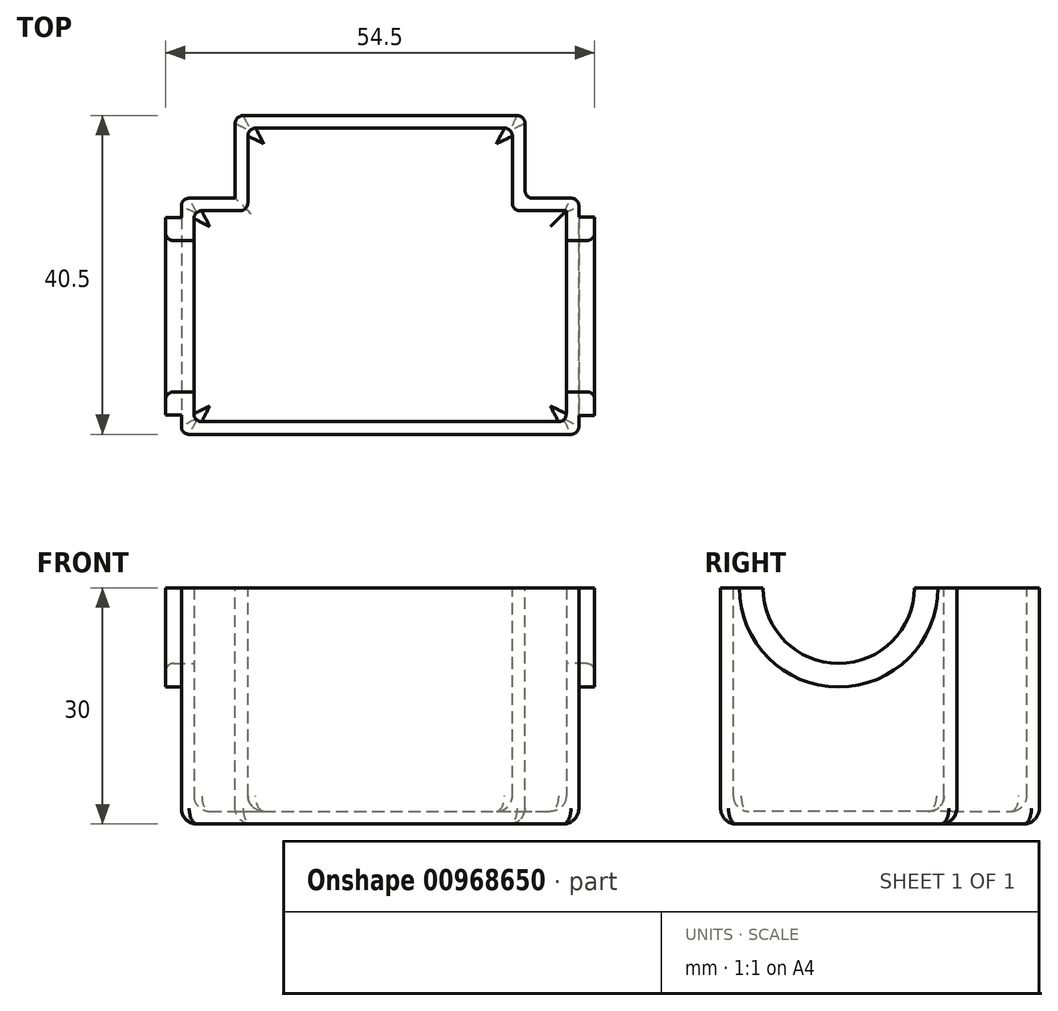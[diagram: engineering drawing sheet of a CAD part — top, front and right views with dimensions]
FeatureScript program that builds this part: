
annotation { "Feature Type Name" : "Feature", "Feature Type Description" : "" }
export const myFeature = defineFeature(function(context is Context, id is Id, definition is map)
    precondition{}
    {
        {
            var Q0;
            Q0=qCreatedBy(makeId("Top.planeOp"),FACE);
            var sketch = newSketch(context, id + "F0", { "sketchPlane" : qUnion([Q0])});
            skLineSegment(sketch, "E0.bottom", {"start": v(-25.25, 15) * mm, "end": v(25.25, 15) * mm});
            skLineSegment(sketch, "E0.top", {"start": v(-25.25, -15) * mm, "end": v(25.25, -15) * mm});
            skLineSegment(sketch, "E0.left", {"start": v(-25.25, 15) * mm, "end": v(-25.25, -15) * mm});
            skLineSegment(sketch, "E0.right", {"start": v(25.25, 15) * mm, "end": v(25.25, -15) * mm});
            skPoint(sketch, "E0.middle", {"position": v(0, 0) * mm});
            skSolve(sketch);
        }
        {
            var Q0;
            Q0=makeQuery(id+"F0.imprint","IMPRINT",FACE,{"disambiguationData":[TD([[makeQuery(id+"F0.imprint","IMPRINT",EDGE,{"derivedFrom":sQuery(id+"F0.wireOp",EDGE,"E0.bottom")}),-1.0]])]});
            extrude(context, id + "F1", {"entities" : qUnion([Q0]), "depth" : 30 * mm, "offsetDistance" : 25 * mm});
        }
        {
            var Q0;
            Q0=makeQuery(id+"F1.opExtrude","CAP_FACE",FACE,{"disambiguationData":[OSD([sQuery(id+"F0.wireOp",EDGE,"E0.bottom"),sQuery(id+"F0.wireOp",EDGE,"E0.top"),sQuery(id+"F0.wireOp",EDGE,"E0.left"),sQuery(id+"F0.wireOp",EDGE,"E0.right")])],"isStart":false});
            var sketch = newSketch(context, id + "F2", { "sketchPlane" : qUnion([Q0])});
            skLineSegment(sketch, "E1.bottom", {"start": v(-18.4, 15) * mm, "end": v(18.4, 15) * mm});
            skLineSegment(sketch, "E1.top", {"start": v(-18.4, 25.5) * mm, "end": v(18.4, 25.5) * mm});
            skLineSegment(sketch, "E1.left", {"start": v(-18.4, 15) * mm, "end": v(-18.4, 25.5) * mm});
            skLineSegment(sketch, "E1.right", {"start": v(18.4, 15) * mm, "end": v(18.4, 25.5) * mm});
            skLineSegment(sketch, "E2", {"start": v(-18.4, 25.5) * mm, "end": v(18.4, 15) * mm, "construction": true});
            skLineSegment(sketch, "E3", {"start": v(-18.4, 25.5) * mm, "end": v(25.25, -15) * mm, "construction": true});
            skLineSegment(sketch, "E4", {"start": v(18.4, 25.5) * mm, "end": v(-25.25, -15) * mm, "construction": true});
            skPoint(sketch, "E5", {"position": v(0, 8.43) * mm});
            skPoint(sketch, "E6", {"position": v(0, 0) * mm});
            skSolve(sketch);
        }
        {
            var Q0;
            Q0=makeQuery(id+"F2.imprint","IMPRINT",FACE,{"disambiguationData":[TD([[makeQuery(id+"F2.imprint","IMPRINT",EDGE,{"derivedFrom":sQuery(id+"F2.wireOp",EDGE,"E1.bottom")}),1.0]])]});
            extrude(context, id + "F3", {"entities" : qUnion([Q0]), "operationType" : NewBodyOperationType.ADD, "oppositeDirection" : true, "depth" : 30 * mm, "offsetDistance" : 25 * mm});
        }
        {
            var Q0;
            Q0=makeQuery(id+"F3.boolean.opBoolean","MERGE",FACE,{"derivedFrom":[makeQuery(id+"F1.opExtrude","CAP_FACE",FACE,{"disambiguationData":[OSD([sQuery(id+"F0.wireOp",EDGE,"E0.bottom"),sQuery(id+"F0.wireOp",EDGE,"E0.top"),sQuery(id+"F0.wireOp",EDGE,"E0.left"),sQuery(id+"F0.wireOp",EDGE,"E0.right")])],"isStart":false}),makeQuery(id+"F3.opExtrude","CAP_FACE",FACE,{"disambiguationData":[OSD([sQuery(id+"F2.wireOp",EDGE,"E1.bottom"),sQuery(id+"F2.wireOp",EDGE,"E1.top"),sQuery(id+"F2.wireOp",EDGE,"E1.left"),sQuery(id+"F2.wireOp",EDGE,"E1.right")])],"isStart":true})]});
            shell(context, id + "F4", {"entities" : qUnion([Q0]), "thickness" : 1.6 * mm});
        }
        {
            var Q0;
            Q0=makeQuery(id+"F1.opExtrude","SWEPT_EDGE",EDGE,{"disambiguationData":[OSD([sQuery(id+"F0.wireOp",EDGE,"E0.bottom"),sQuery(id+"F0.wireOp",EDGE,"E0.left")])]});
            var Q1;
            Q1=makeQuery(id+"F1.opExtrude","SWEPT_EDGE",EDGE,{"disambiguationData":[OSD([sQuery(id+"F0.wireOp",EDGE,"E0.top"),sQuery(id+"F0.wireOp",EDGE,"E0.left")])]});
            var Q2;
            Q2=makeQuery(id+"F4.opShell","OFFSET_EDGE",EDGE,{"disambiguationData":[OSD([sQuery(id+"F0.wireOp",EDGE,"E0.top"),sQuery(id+"F0.wireOp",EDGE,"E0.right")])]});
            var Q3;
            Q3=makeQuery(id+"F1.opExtrude","SWEPT_EDGE",EDGE,{"disambiguationData":[OSD([sQuery(id+"F0.wireOp",EDGE,"E0.top"),sQuery(id+"F0.wireOp",EDGE,"E0.right")])]});
            var Q4;
            Q4=makeQuery(id+"F1.opExtrude","SWEPT_EDGE",EDGE,{"disambiguationData":[OSD([sQuery(id+"F0.wireOp",EDGE,"E0.bottom"),sQuery(id+"F0.wireOp",EDGE,"E0.right")])]});
            var Q5;
            Q5=makeQuery(id+"F4.opShell","OFFSET_EDGE",EDGE,{"disambiguationData":[OSD([sQuery(id+"F0.wireOp",EDGE,"E0.bottom"),sQuery(id+"F2.wireOp",EDGE,"E1.bottom"),sQuery(id+"F2.wireOp",EDGE,"E1.left")])]});
            var Q6;
            Q6=makeQuery(id+"F4.opShell","OFFSET_EDGE",EDGE,{"disambiguationData":[OSD([sQuery(id+"F0.wireOp",EDGE,"E0.bottom"),sQuery(id+"F2.wireOp",EDGE,"E1.bottom"),sQuery(id+"F2.wireOp",EDGE,"E1.right")])]});
            var Q7;
            Q7=makeQuery(id+"F3.opExtrude","SWEPT_EDGE",EDGE,{"disambiguationData":[OSD([sQuery(id+"F0.wireOp",EDGE,"E0.bottom"),sQuery(id+"F2.wireOp",EDGE,"E1.bottom"),sQuery(id+"F2.wireOp",EDGE,"E1.right")])]});
            var Q8;
            Q8=makeQuery(id+"F4.opShell","OFFSET_EDGE",EDGE,{"disambiguationData":[OSD([sQuery(id+"F2.wireOp",EDGE,"E1.top"),sQuery(id+"F2.wireOp",EDGE,"E1.right")])]});
            var Q9;
            Q9=makeQuery(id+"F3.opExtrude","SWEPT_EDGE",EDGE,{"disambiguationData":[OSD([sQuery(id+"F2.wireOp",EDGE,"E1.top"),sQuery(id+"F2.wireOp",EDGE,"E1.right")])]});
            var Q10;
            Q10=makeQuery(id+"F4.opShell","OFFSET_EDGE",EDGE,{"disambiguationData":[OSD([sQuery(id+"F2.wireOp",EDGE,"E1.top"),sQuery(id+"F2.wireOp",EDGE,"E1.left")])]});
            var Q11;
            Q11=makeQuery(id+"F3.opExtrude","SWEPT_EDGE",EDGE,{"disambiguationData":[OSD([sQuery(id+"F2.wireOp",EDGE,"E1.top"),sQuery(id+"F2.wireOp",EDGE,"E1.left")])]});
            var Q12;
            Q12=makeQuery(id+"F3.opExtrude","SWEPT_EDGE",EDGE,{"disambiguationData":[OSD([sQuery(id+"F0.wireOp",EDGE,"E0.bottom"),sQuery(id+"F2.wireOp",EDGE,"E1.bottom"),sQuery(id+"F2.wireOp",EDGE,"E1.left")])]});
            var Q13;
            Q13=makeQuery(id+"F4.opShell","OFFSET_EDGE",EDGE,{"disambiguationData":[OSD([sQuery(id+"F0.wireOp",EDGE,"E0.bottom"),sQuery(id+"F0.wireOp",EDGE,"E0.left")])]});
            var Q14;
            Q14=makeQuery(id+"F4.opShell","OFFSET_EDGE",EDGE,{"disambiguationData":[OSD([sQuery(id+"F0.wireOp",EDGE,"E0.top"),sQuery(id+"F0.wireOp",EDGE,"E0.left")])]});
            fillet(context, id + "F5", {"entities" : qUnion([Q0, Q1, Q2, Q3, Q4, Q5, Q6, Q7, Q8, Q9, Q10, Q11, Q12, Q13, Q14]), "radius" : 1 * mm, "tangentPropagation" : true, "allowEdgeOverflow" : false});
        }
        {
            var Q0;
            Q0=makeQuery(id+"F1.opExtrude","CAP_EDGE",EDGE,{"disambiguationData":[OSD([sQuery(id+"F0.wireOp",EDGE,"E0.right")])],"isStart":true});
            var Q1;
            {var subQ0=sQuery(id+"F0.wireOp",EDGE,"E0.right");Q1=makeQuery(id+"F4.opShell","OFFSET_EDGE",EDGE,{"disambiguationData":[OSD([subQ0]),TDD([makeQuery(id+"F1.opExtrude","CAP_EDGE",EDGE,{"disambiguationData":[OSD([subQ0])],"isStart":true})])]});}
            fillet(context, id + "F6", {"entities" : qUnion([Q0, Q1]), "radius" : 2 * mm, "tangentPropagation" : true, "allowEdgeOverflow" : false});
        }
        {
            var Q0;
            Q0=makeQuery(id+"F1.opExtrude","SWEPT_FACE",FACE,{"disambiguationData":[OSD([sQuery(id+"F0.wireOp",EDGE,"E0.right")])]});
            var sketch = newSketch(context, id + "F7", { "sketchPlane" : qUnion([Q0])});
            skCircle(sketch, "E7", {"center": v(0, 30) * mm, "radius": 9.6 * mm});
            skCircle(sketch, "E8.0", {"center": v(0, 30) * mm, "radius": 12.6 * mm});
            skLineSegment(sketch, "E9", {"start": v(12.6, 30) * mm, "end": v(-12.6, 30) * mm});
            skSolve(sketch);
        }
        {
            var Q0;
            {var subQ0=sQuery(id+"F7.wireOp",EDGE,"E9");var subQ1=sQuery(id+"F7.wireOp",EDGE,"E7");var subQ2=makeQuery(id+"F7.imprint","INTERSECT",VERTEX,{"disambiguationData":[OD(0.0)],"derivedFrom":[subQ1,subQ0]});Q0=makeQuery(id+"F7.imprint","IMPRINT",FACE,{"disambiguationData":[TD([[makeQuery(id+"F7.imprint","IMPRINT",EDGE,{"disambiguationData":[TD([[subQ2,1.0]])],"derivedFrom":subQ1}),-1.0]])]});}
            extrude(context, id + "F8", {"entities" : qUnion([Q0]), "operationType" : NewBodyOperationType.ADD, "depth" : 2 * mm, "offsetDistance" : 25 * mm});
        }
        {
            var Q0;
            {var subQ0=sQuery(id+"F7.wireOp",EDGE,"E7");var subQ3=sQuery(id+"F0.wireOp",EDGE,"E0.right");Q0=makeQuery(id+"F8.boolean.opBoolean","SPLIT",FACE,{"disambiguationData":[TD([makeQuery(id+"F8.opExtrude","SWEPT_FACE",FACE,{"disambiguationData":[OSD([subQ0])]})])],"derivedFrom":makeQuery(id+"F1.opExtrude","SWEPT_FACE",FACE,{"disambiguationData":[OSD([subQ3])]})});}
            extrude(context, id + "F9", {"entities" : qUnion([Q0]), "operationType" : NewBodyOperationType.REMOVE, "endBound" : BoundingType.THROUGH_ALL, "oppositeDirection" : true, "depth" : 25 * mm, "offsetDistance" : 25 * mm});
        }
        {
            var Q0;
            Q0=makeQuery(id+"F1.opExtrude","SWEPT_FACE",FACE,{"disambiguationData":[OSD([sQuery(id+"F0.wireOp",EDGE,"E0.left")])]});
            var sketch = newSketch(context, id + "F10", { "sketchPlane" : qUnion([Q0])});
            skCircle(sketch, "E10", {"center": v(0, 30) * mm, "radius": 9.56 * mm});
            skCircle(sketch, "E11.0", {"center": v(0, 30) * mm, "radius": 12.56 * mm});
            skLineSegment(sketch, "E12", {"start": v(-12.56, 30) * mm, "end": v(12.56, 30) * mm});
            skSolve(sketch);
        }
        {
            var Q0;
            {var subQ2=sQuery(id+"F0.wireOp",EDGE,"E0.left");var subQ8=makeQuery(id+"F1.opExtrude","SWEPT_FACE",FACE,{"disambiguationData":[OSD([subQ2])]});var subQ9=sQuery(id+"F7.wireOp",EDGE,"E7");var subQ10=makeQuery(id+"F9.opExtrude","SWEPT_FACE",FACE,{"disambiguationData":[OSD([subQ9])]});var subQ19=makeQuery(id+"F9.boolean.opBoolean","INTERSECT",EDGE,{"derivedFrom":[subQ8,subQ10]});Q0=makeQuery(id+"F10.imprint","IMPRINT",FACE,{"disambiguationData":[TD([[makeQuery(id+"F10.imprint","IMPRINT",EDGE,{"derivedFrom":subQ19}),1.0]])]});}
            extrude(context, id + "F11", {"entities" : qUnion([Q0]), "operationType" : NewBodyOperationType.ADD, "depth" : 2 * mm, "offsetDistance" : 25 * mm});
        }
        {
            var Q0;
            Q0=makeQuery(id+"F8.opExtrude","CAP_EDGE",EDGE,{"disambiguationData":[OSD([sQuery(id+"F7.wireOp",EDGE,"E7")])],"isStart":false});
            var Q1;
            Q1=makeQuery(id+"F11.opExtrude","CAP_EDGE",EDGE,{"disambiguationData":[OSD([sQuery(id+"F0.wireOp",EDGE,"E0.left"),sQuery(id+"F7.wireOp",EDGE,"E7")])],"isStart":false});
            fillet(context, id + "F12", {"entities" : qUnion([Q0, Q1]), "radius" : 1 * mm, "tangentPropagation" : true, "allowEdgeOverflow" : false});
        }
    });
